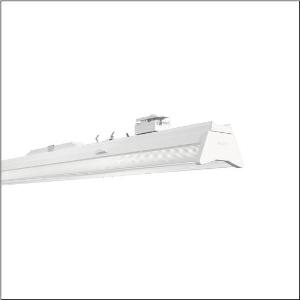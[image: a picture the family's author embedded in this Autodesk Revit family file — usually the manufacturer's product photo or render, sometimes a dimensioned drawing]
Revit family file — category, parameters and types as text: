
# Revit family: licross_r__21_performance_mo_52td167n46xg_c3aa
name_source: partatom
category: Lighting Fixtures
units: mm (PartAtom-declared; Revit-internal decimal feet)

## family parameters
Cut with Voids When Loaded = No
Host = Face
Light Source = No
Part Type = Normal
Room Calculation Point = No
Round Connector Dimension = Use Diameter
Shared = No

## types (1)
- Licross® 21 Performance MO (1 x LED, 6000 lm, 32.4 W, 4000K)
    Apparent Load = 32 VA
    CIE Flux Codes = 66 88 96 79 100
    Color Rendering = 80
    Color Temperature = 4000K
    Default Elevation = 1800 mm
    Description = Licross® 21 Performance MO, luminaire insert, of sheet steel, galvanised, coil coated, white, length: 1.500mm, width: 120mm, height: 123mm, LED rated luminous flux: 6.000lm, light colour: 840, control gear: ON/OFF, with plug, 3-pole, with phase selection, mains connection: 220..240V, AC, 50/60Hz, rated input power: 32W, halogen-free wiring, primary light control with lens, of plastic, primary optical cover: cover, of PMMA, light emission: direct/indirect distribution, primary light characteristic: symmetric, protection rating (complete): IP54, insulation class (complete): insulation class I (protective earthing), certification: CE, ENEC, UKCA, protection symbol: D if used in an environment with non-conductive dust loads with corresponding accessories, impact resistance: IK06, permissible ambient temperature for indoor applications: -35..+50°C, corresponds to IFS (International Featured Standards) requirements for safety and quality in the food industry, reducing of maximum allowable ambient temperature of 5°C with ceiling mounting, LABS conformity tested according to VDMA 24364:2018-05, packaging unit: 1 piece
    Height = 114 mm
    Lamp = 1 x LED
    Lamp Light Flux = 6000 lm
    Lamp Power = 32.4 W
    Lamp count = 1
    Length = 1500 mm
    Luminous efficacy = 185 lm/W
    Manufacturer = Siteco
    ModVariant = No
    Model = 52TD167N46XG
    Mounting Place = Ceiling
    Mounting Type = Pendant
    Number of Poles = 1
    OnlyDefault = Yes
    Power Factor = 1
    Product Name = Licross® 21 Performance MO
    Product group = luminaire insert
    ProductGroupID = 901
    Protection Class = Protection class I
    Protection Degree = IP 54
    RLX_Detail_Level = 1
    RLX_Emergency_Light_Flux = 0 lm
    RLX_Emergency_Type = 0
    RLX_Emergency_Type_DB = No
    RlxData = <blob elided: 30445 chars, md5=db7f2458>
    Socket = socket
    Standby Power = 0 W
    System Light Flux = 6000 lm
    System Power = 32 W
    Type Comments = Product without accessories
    Type Image = l_1256138.jpg
    URL = http://relux.com
    VarID = ---
    Voltage = 0 V
    Weight = 0.00 kg
    Width = 120 mm

## geometry (parser evidence)
native form markers: Blend x4, Sweep x13
no freeform markers — native parametric forms only
